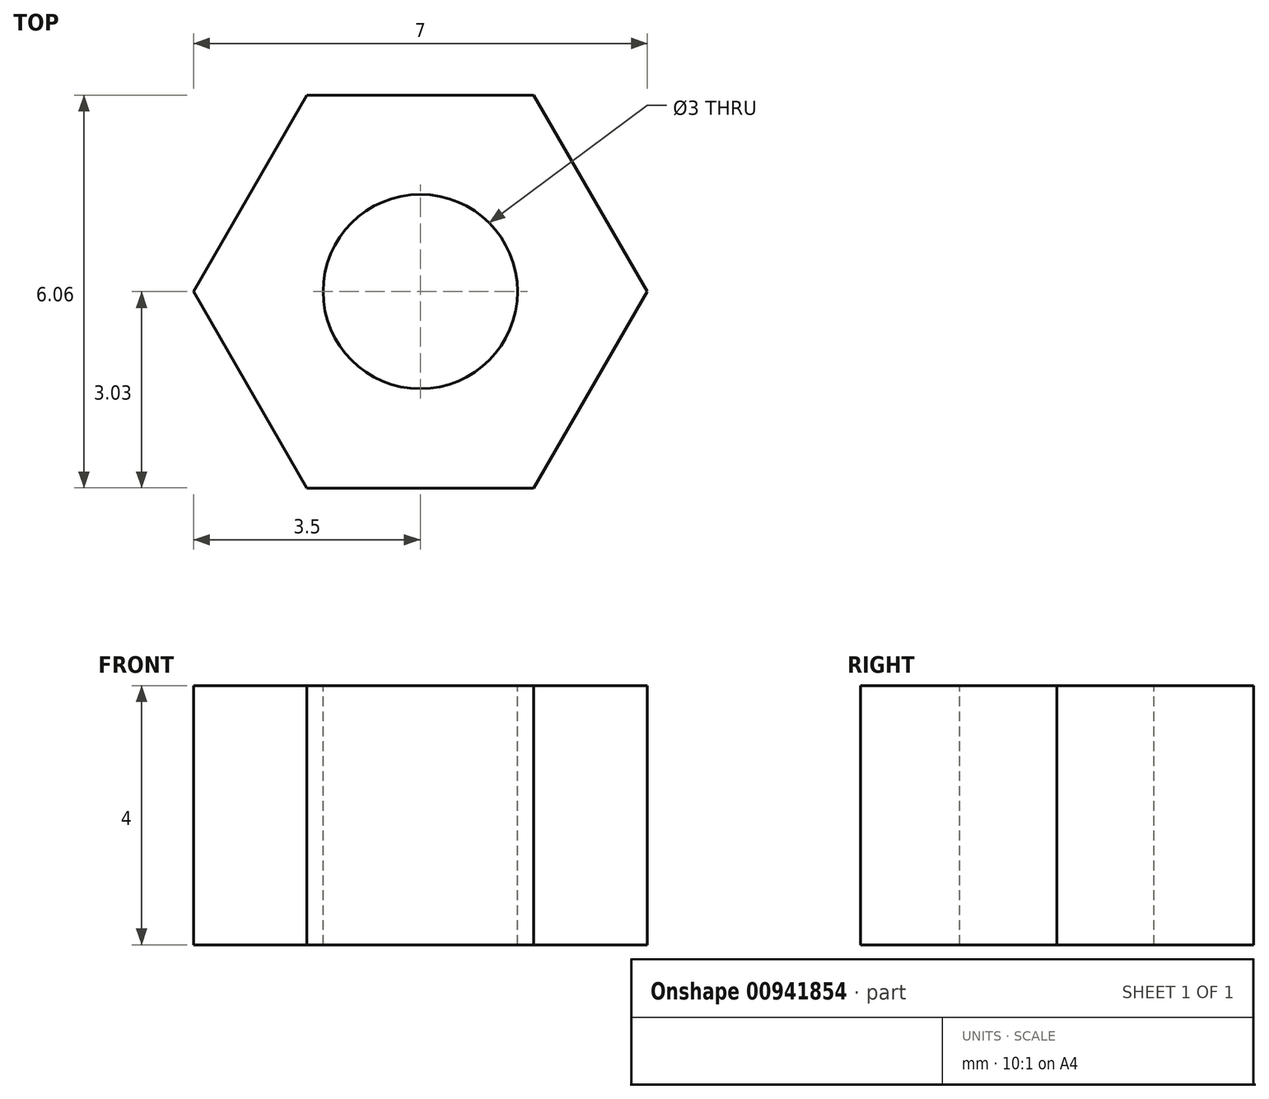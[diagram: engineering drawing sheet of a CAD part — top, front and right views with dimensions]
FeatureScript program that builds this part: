
annotation { "Feature Type Name" : "Feature", "Feature Type Description" : "" }
export const myFeature = defineFeature(function(context is Context, id is Id, definition is map)
    precondition{}
    {
        {
            var Q0;
            Q0=qCreatedBy(makeId("Top.planeOp"),FACE);
            var sketch = newSketch(context, id + "F0", { "sketchPlane" : qUnion([Q0])});
            skCircle(sketch, "E0.cCircle", {"center": v(0, 0) * mm, "radius": 3.03 * mm, "construction": true});
            skLineSegment(sketch, "E0.0", {"start": v(-1.75, 3.03) * mm, "end": v(1.75, 3.03) * mm});
            skLineSegment(sketch, "E0.1", {"start": v(1.75, 3.03) * mm, "end": v(3.5, 0) * mm});
            skLineSegment(sketch, "E0.2", {"start": v(3.5, 0) * mm, "end": v(1.75, -3.03) * mm});
            skLineSegment(sketch, "E0.3", {"start": v(1.75, -3.03) * mm, "end": v(-1.75, -3.03) * mm});
            skLineSegment(sketch, "E0.4", {"start": v(-1.75, -3.03) * mm, "end": v(-3.5, 0) * mm});
            skLineSegment(sketch, "E0.5", {"start": v(-3.5, 0) * mm, "end": v(-1.75, 3.03) * mm});
            skPoint(sketch, "E0.0.midPoint", {"position": v(0, 3.03) * mm});
            skCircle(sketch, "E1", {"center": v(0, 0) * mm, "radius": 1.5 * mm});
            skSolve(sketch);
        }
        {
            var Q0;
            Q0 = qSketchRegion(id + "F0", true);
            extrude(context, id + "F1", {"entities" : qUnion([Q0]), "oppositeDirection" : true, "depth" : 2 * mm, "offsetDistance" : 25.4 * mm, "hasSecondDirection" : true, "secondDirectionOppositeDirection" : false, "secondDirectionDepth" : 2 * mm});
        }
    });
